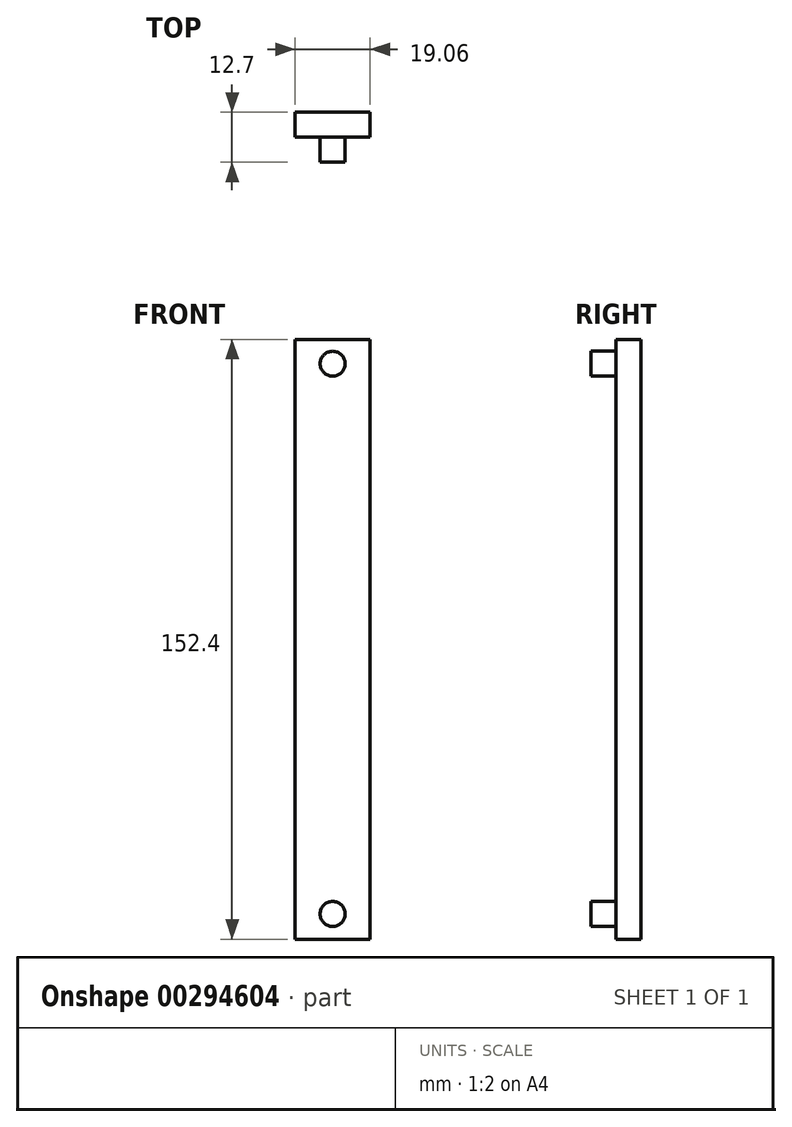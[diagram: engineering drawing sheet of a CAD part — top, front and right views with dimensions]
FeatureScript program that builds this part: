
annotation { "Feature Type Name" : "Feature", "Feature Type Description" : "" }
export const myFeature = defineFeature(function(context is Context, id is Id, definition is map)
    precondition{}
    {
        {
            var Q0;
            Q0=qCreatedBy(makeId("Front.planeOp"),FACE);
            var sketch = newSketch(context, id + "F0", { "sketchPlane" : qUnion([Q0])});
            skLineSegment(sketch, "E0.bottom", {"start": v(9.53, 76.2) * mm, "end": v(-9.52, 76.2) * mm});
            skLineSegment(sketch, "E0.top", {"start": v(9.53, -76.2) * mm, "end": v(-9.53, -76.2) * mm});
            skLineSegment(sketch, "E0.left", {"start": v(9.53, 76.2) * mm, "end": v(9.53, -76.2) * mm});
            skLineSegment(sketch, "E0.right", {"start": v(-9.52, 76.2) * mm, "end": v(-9.53, -76.2) * mm});
            skPoint(sketch, "E0.middle", {"position": v(0, 0) * mm});
            skCircle(sketch, "E1", {"center": v(0, 70.02) * mm, "radius": 3.18 * mm});
            skCircle(sketch, "E2", {"center": v(0, -69.77) * mm, "radius": 3.18 * mm});
            skSolve(sketch);
        }
        {
            var Q0;
            Q0=makeQuery(id+"F0.imprint","IMPRINT",FACE,{"disambiguationData":[TD([[makeQuery(id+"F0.imprint","IMPRINT",EDGE,{"derivedFrom":sQuery(id+"F0.wireOp",EDGE,"E1")}),1.0]])]});
            var Q1;
            Q1=makeQuery(id+"F0.imprint","IMPRINT",FACE,{"disambiguationData":[TD([[makeQuery(id+"F0.imprint","IMPRINT",EDGE,{"derivedFrom":sQuery(id+"F0.wireOp",EDGE,"E0.bottom")}),1.0]])]});
            var Q2;
            Q2=makeQuery(id+"F0.imprint","IMPRINT",FACE,{"disambiguationData":[TD([[makeQuery(id+"F0.imprint","IMPRINT",EDGE,{"derivedFrom":sQuery(id+"F0.wireOp",EDGE,"E2")}),1.0]])]});
            extrude(context, id + "F1", {"entities" : qUnion([Q0, Q1, Q2]), "depth" : 6.35 * mm});
        }
        {
            var Q0;
            Q0=makeQuery(id+"F0.imprint","IMPRINT",FACE,{"disambiguationData":[TD([[makeQuery(id+"F0.imprint","IMPRINT",EDGE,{"derivedFrom":sQuery(id+"F0.wireOp",EDGE,"E1")}),1.0]])]});
            var Q1;
            Q1=makeQuery(id+"F0.imprint","IMPRINT",FACE,{"disambiguationData":[TD([[makeQuery(id+"F0.imprint","IMPRINT",EDGE,{"derivedFrom":sQuery(id+"F0.wireOp",EDGE,"E2")}),1.0]])]});
            extrude(context, id + "F2", {"entities" : qUnion([Q0, Q1]), "operationType" : NewBodyOperationType.ADD, "depth" : 12.7 * mm});
        }
    });
